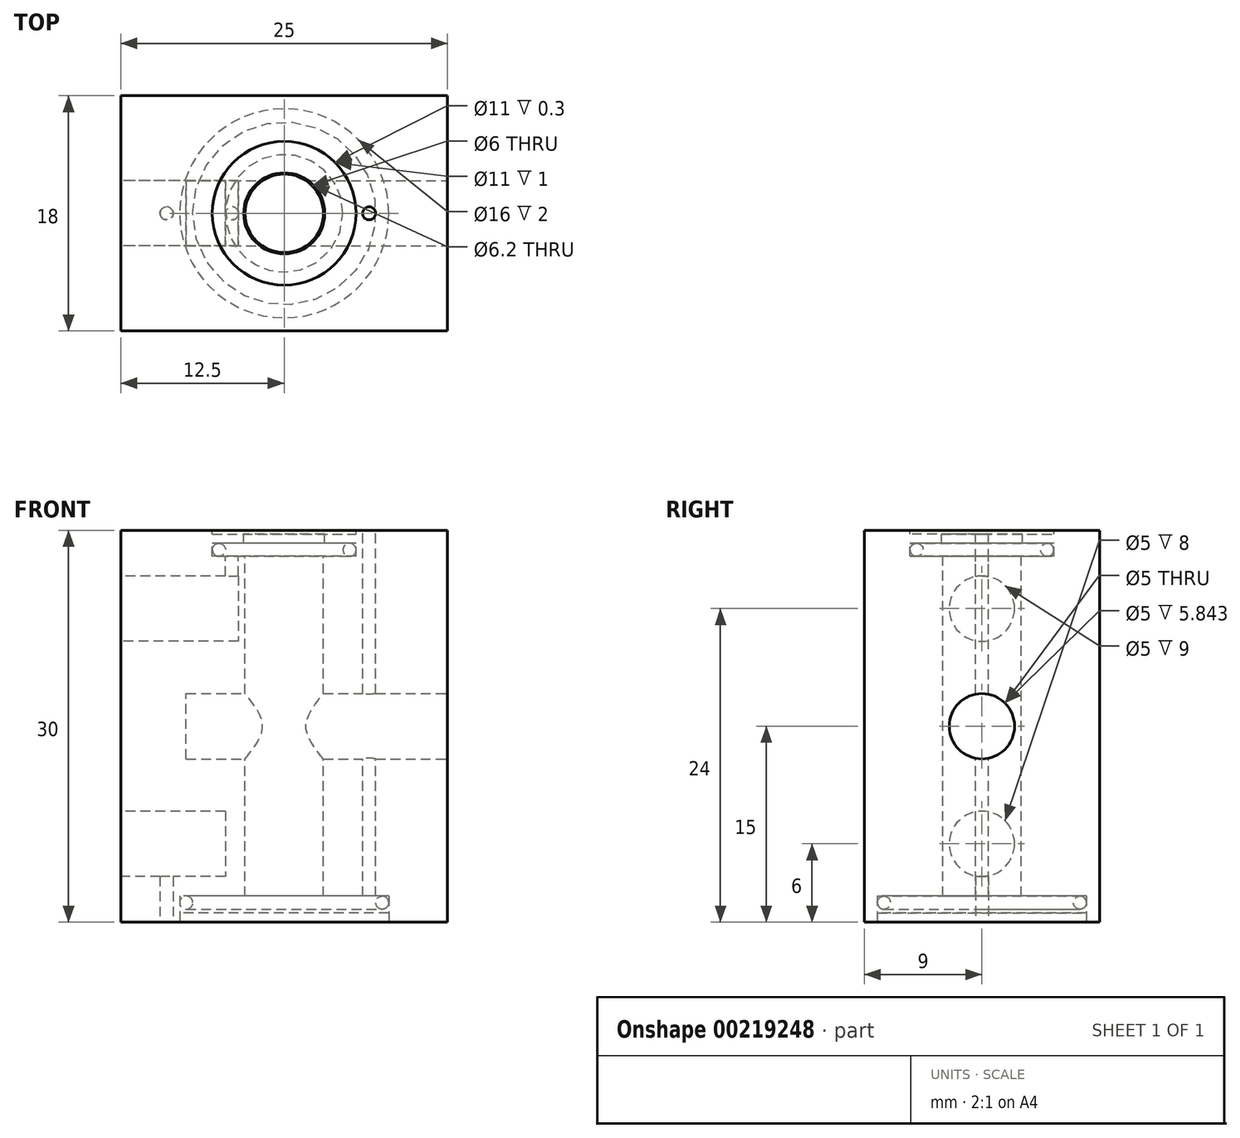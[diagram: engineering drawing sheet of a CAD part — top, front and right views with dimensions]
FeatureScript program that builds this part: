
annotation { "Feature Type Name" : "Feature", "Feature Type Description" : "" }
export const myFeature = defineFeature(function(context is Context, id is Id, definition is map)
    precondition{}
    {
        {
            var Q0;
            Q0=qCreatedBy(makeId("Front.planeOp"),FACE);
            var sketch = newSketch(context, id + "F0", { "sketchPlane" : qUnion([Q0])});
            skLineSegment(sketch, "E0.bottom", {"start": v(0, 0) * mm, "end": v(25, 0) * mm});
            skLineSegment(sketch, "E0.top", {"start": v(0, 30) * mm, "end": v(25, 30) * mm});
            skLineSegment(sketch, "E0.left", {"start": v(0, 0) * mm, "end": v(0, 30) * mm});
            skLineSegment(sketch, "E0.right", {"start": v(25, 0) * mm, "end": v(25, 30) * mm});
            skSolve(sketch);
        }
        {
            var Q0;
            Q0 = qSketchRegion(id + "F0", true);
            extrude(context, id + "F1", {"entities" : qUnion([Q0]), "endBound" : BoundingType.SYMMETRIC, "depth" : 18 * mm});
        }
        {
            var Q0;
            Q0=makeQuery(id+"F1.opExtrude","SWEPT_FACE",FACE,{"disambiguationData":[OSD([sQuery(id+"F0.wireOp",EDGE,"E0.right")])]});
            var sketch = newSketch(context, id + "F12", { "sketchPlane" : qUnion([Q0])});
            skLineSegment(sketch, "E1", {"start": v(0, 30) * mm, "end": v(0, 0) * mm, "construction": true});
            skCircle(sketch, "E2", {"center": v(0, 15) * mm, "radius": 2.5 * mm});
            skSolve(sketch);
        }
        {
            var Q0;
            Q0 = qSketchRegion(id + "F12", true);
            extrude(context, id + "F2", {"entities" : qUnion([Q0]), "operationType" : NewBodyOperationType.REMOVE, "oppositeDirection" : true, "depth" : 20 * mm});
        }
        {
            var Q0;
            Q0=makeQuery(id+"F1.opExtrude","SWEPT_FACE",FACE,{"disambiguationData":[OSD([sQuery(id+"F0.wireOp",EDGE,"E0.top")])]});
            var sketch = newSketch(context, id + "F13", { "sketchPlane" : qUnion([Q0])});
            skLineSegment(sketch, "E3", {"start": v(0, 0) * mm, "end": v(25, 0) * mm, "construction": true});
            skCircle(sketch, "E4", {"center": v(12.5, 0) * mm, "radius": 3 * mm});
            skCircle(sketch, "E5", {"center": v(19, 0) * mm, "radius": 0.5 * mm});
            skCircle(sketch, "E6", {"center": v(8.5, 0) * mm, "radius": 0.5 * mm});
            skCircle(sketch, "E7", {"center": v(12.5, 0) * mm, "radius": 8 * mm});
            skCircle(sketch, "E8", {"center": v(12.5, 0) * mm, "radius": 5.5 * mm});
            skSolve(sketch);
        }
        {
            var Q0;
            Q0=makeQuery(id+"F13.imprint","IMPRINT",FACE,{"disambiguationData":[TD([[makeQuery(id+"F13.imprint","IMPRINT",EDGE,{"derivedFrom":sQuery(id+"F13.wireOp",EDGE,"E4")}),1.0]])]});
            extrude(context, id + "F3", {"entities" : qUnion([Q0]), "operationType" : NewBodyOperationType.REMOVE, "endBound" : BoundingType.THROUGH_ALL, "oppositeDirection" : true, "depth" : 25 * mm});
        }
        {
            var Q0;
            Q0=makeQuery(id+"F13.imprint","IMPRINT",FACE,{"disambiguationData":[TD([[makeQuery(id+"F13.imprint","IMPRINT",EDGE,{"derivedFrom":sQuery(id+"F13.wireOp",EDGE,"E5")}),1.0]])]});
            var Q1;
            Q1=sQuery(id+"F13.wireOp",EDGE,"E5");
            extrude(context, id + "F14", {"entities" : qUnion([Q0]), "operationType" : NewBodyOperationType.REMOVE, "surfaceEntities" : qUnion([Q1]), "endBound" : BoundingType.THROUGH_ALL, "oppositeDirection" : true, "depth" : 25 * mm});
        }
        {
            var Q0;
            Q0=makeQuery(id+"F1.opExtrude","SWEPT_FACE",FACE,{"disambiguationData":[OSD([sQuery(id+"F0.wireOp",EDGE,"E0.left")])]});
            var sketch = newSketch(context, id + "F4", { "sketchPlane" : qUnion([Q0])});
            skLineSegment(sketch, "E9", {"start": v(0, 30) * mm, "end": v(0, 0) * mm, "construction": true});
            skCircle(sketch, "E10", {"center": v(0, 6) * mm, "radius": 2.5 * mm});
            skCircle(sketch, "E11", {"center": v(0, 24) * mm, "radius": 2.5 * mm});
            skSolve(sketch);
        }
        {
            var Q0;
            Q0=makeQuery(id+"F4.imprint","IMPRINT",FACE,{"disambiguationData":[TD([[makeQuery(id+"F4.imprint","IMPRINT",EDGE,{"derivedFrom":sQuery(id+"F4.wireOp",EDGE,"E10")}),1.0]])]});
            var Q1;
            Q1=sQuery(id+"F4.wireOp",EDGE,"E10");
            extrude(context, id + "F5", {"entities" : qUnion([Q0]), "operationType" : NewBodyOperationType.REMOVE, "surfaceEntities" : qUnion([Q1]), "oppositeDirection" : true, "depth" : 8 * mm});
        }
        {
            var Q0;
            Q0=qCreatedBy(makeId("Top.planeOp"),FACE);
            var sketch = newSketch(context, id + "F6", { "sketchPlane" : qUnion([Q0])});
            skCircle(sketch, "E12", {"center": v(3.5, 0) * mm, "radius": 0.5 * mm});
            skCircle(sketch, "E13.0", {"center": v(12.5, 0) * mm, "radius": 8 * mm});
            skSolve(sketch);
        }
        {
            var Q0;
            Q0=makeQuery(id+"F6.imprint","IMPRINT",FACE,{"disambiguationData":[TD([[makeQuery(id+"F6.imprint","IMPRINT",EDGE,{"derivedFrom":sQuery(id+"F6.wireOp",EDGE,"E12")}),1.0]])]});
            extrude(context, id + "F15", {"entities" : qUnion([Q0]), "operationType" : NewBodyOperationType.REMOVE, "endBound" : BoundingType.UP_TO_NEXT, "depth" : 25 * mm});
        }
        {
            var Q0;
            Q0=makeQuery(id+"F4.imprint","IMPRINT",FACE,{"disambiguationData":[TD([[makeQuery(id+"F4.imprint","IMPRINT",EDGE,{"derivedFrom":sQuery(id+"F4.wireOp",EDGE,"E11")}),1.0]])]});
            var Q1;
            Q1=sQuery(id+"F4.wireOp",EDGE,"E11");
            extrude(context, id + "F7", {"entities" : qUnion([Q0]), "operationType" : NewBodyOperationType.REMOVE, "surfaceEntities" : qUnion([Q1]), "oppositeDirection" : true, "depth" : 9 * mm});
        }
        {
            var Q0;
            Q0=makeQuery(id+"F13.imprint","IMPRINT",FACE,{"disambiguationData":[TD([[makeQuery(id+"F13.imprint","IMPRINT",EDGE,{"derivedFrom":sQuery(id+"F13.wireOp",EDGE,"E6")}),1.0]])]});
            extrude(context, id + "F16", {"entities" : qUnion([Q0]), "operationType" : NewBodyOperationType.REMOVE, "endBound" : BoundingType.UP_TO_NEXT, "oppositeDirection" : true, "depth" : 25 * mm});
        }
        {
            var Q0;
            Q0=makeQuery(id+"F13.imprint","IMPRINT",FACE,{"disambiguationData":[TD([[makeQuery(id+"F13.imprint","IMPRINT",EDGE,{"derivedFrom":sQuery(id+"F13.wireOp",EDGE,"E4")}),-1.0]])]});
            var Q1;
            Q1=sQuery(id+"F13.wireOp",EDGE,"E8");
            extrude(context, id + "F8", {"entities" : qUnion([Q0]), "operationType" : NewBodyOperationType.REMOVE, "surfaceEntities" : qUnion([Q1]), "oppositeDirection" : true, "depth" : 2 * mm});
        }
        {
            var Q0;
            Q0=makeQuery(id+"F6.imprint","IMPRINT",FACE,{"disambiguationData":[TD([[makeQuery(id+"F6.imprint","IMPRINT",EDGE,{"derivedFrom":sQuery(id+"F6.wireOp",EDGE,"E13.0")}),1.0]])]});
            var Q1;
            Q1=sQuery(id+"F6.wireOp",EDGE,"E13.0");
            extrude(context, id + "F9", {"entities" : qUnion([Q0]), "operationType" : NewBodyOperationType.REMOVE, "surfaceEntities" : qUnion([Q1]), "depth" : 2 * mm});
        }
        {
            var Q0;
            Q0=qCreatedBy(makeId("Front.planeOp"),FACE);
            var sketch = newSketch(context, id + "F10", { "sketchPlane" : qUnion([Q0])});
            skLineSegment(sketch, "E14", {"start": v(18, 30) * mm, "end": v(18, 28) * mm, "construction": true});
            skLineSegment(sketch, "E15", {"start": v(7, 28.5) * mm, "end": v(7, 30) * mm, "construction": true});
            skLineSegment(sketch, "E16.0.0", {"start": v(9.5, 28) * mm, "end": v(15.5, 28) * mm, "construction": true});
            skPoint(sketch, "E17.visualSharp", {"position": v(7, 28) * mm});
            skArc(sketch, "E17.filletArc", {"start": v(7, 28.5) * mm, "mid": v(7.15, 28.15) * mm, "end": v(7.5, 28) * mm, "construction": true});
            skCircle(sketch, "E18", {"center": v(7.5, 28.5) * mm, "radius": 0.5 * mm});
            skLineSegment(sketch, "E19", {"start": v(7, 30) * mm, "end": v(18, 30) * mm, "construction": true});
            skLineSegment(sketch, "E20", {"start": v(15.5, 28) * mm, "end": v(15.5, 2) * mm, "construction": true});
            skLineSegment(sketch, "E21", {"start": v(9.5, 2) * mm, "end": v(9.5, 28) * mm, "construction": true});
            skLineSegment(sketch, "E22", {"start": v(7, 28) * mm, "end": v(18, 28) * mm, "construction": true});
            skPoint(sketch, "E23.orphan", {"position": v(18, 28) * mm});
            skLineSegment(sketch, "E24", {"start": v(12.5, 30) * mm, "end": v(12.5, 28) * mm, "construction": true});
            skLineSegment(sketch, "E25", {"start": v(4.5, 0) * mm, "end": v(4.5, 1.94) * mm, "construction": true});
            skLineSegment(sketch, "E26", {"start": v(20.5, 2) * mm, "end": v(20.5, 0) * mm, "construction": true});
            skLineSegment(sketch, "E27", {"start": v(9.5, 2) * mm, "end": v(15.5, 2) * mm, "construction": true});
            skLineSegment(sketch, "E28", {"start": v(9.5, 2) * mm, "end": v(4.5, 2) * mm, "construction": true});
            skLineSegment(sketch, "E29", {"start": v(20.5, 0) * mm, "end": v(4.5, 0) * mm, "construction": true});
            skLineSegment(sketch, "E30", {"start": v(12.5, 0) * mm, "end": v(12.5, 2) * mm, "construction": true});
            skPoint(sketch, "E31.visualSharp", {"position": v(4.5, 2) * mm});
            skArc(sketch, "E31.filletArc", {"start": v(5, 2) * mm, "mid": v(4.65, 1.85) * mm, "end": v(4.5, 1.5) * mm, "construction": true});
            skCircle(sketch, "E32", {"center": v(5, 1.5) * mm, "radius": 0.5 * mm});
            skLineSegment(sketch, "E33", {"start": v(7, 29) * mm, "end": v(9.4, 29) * mm});
            skPoint(sketch, "E33.endSnap0", {"position": v(18, 29) * mm});
            skLineSegment(sketch, "E34", {"start": v(7, 29) * mm, "end": v(7, 29.7) * mm});
            skLineSegment(sketch, "E35", {"start": v(7, 29.7) * mm, "end": v(9.4, 29.7) * mm});
            skLineSegment(sketch, "E36", {"start": v(18, 29.7) * mm, "end": v(18, 29) * mm});
            skLineSegment(sketch, "E37", {"start": v(9.4, 29.7) * mm, "end": v(9.4, 29) * mm});
            skLineSegment(sketch, "E38.trimOffspring", {"start": v(12.5, 29.7) * mm, "end": v(18, 29.7) * mm});
            skLineSegment(sketch, "E39.trimOffspring", {"start": v(12.5, 29) * mm, "end": v(18, 29) * mm});
            skLineSegment(sketch, "E40", {"start": v(12.52, 1) * mm, "end": v(12.5, 1) * mm});
            skSolve(sketch);
        }
        {
            var Q0;
            Q0=makeQuery(id+"F10.imprint","IMPRINT",FACE,{"disambiguationData":[TD([[makeQuery(id+"F10.imprint","IMPRINT",EDGE,{"derivedFrom":sQuery(id+"F10.wireOp",EDGE,"E18")}),1.0]])]});
            var Q1;
            Q1=sQuery(id+"F10.wireOp",EDGE,"E24");
            revolve(context, id + "F17", {"entities" : qUnion([Q0]), "axis" : qUnion([Q1]), "revolveType" : RevolveType.FULL});
        }
        {
            var Q0;
            {var subQ0=sQuery(id+"F10.wireOp",EDGE,"E34");Q0=makeQuery(id+"F10.imprint","IMPRINT",FACE,{"disambiguationData":[TD([[makeQuery(id+"F10.imprint","IMPRINT",EDGE,{"derivedFrom":subQ0}),-1.0]])]});}
            var Q1;
            Q1=sQuery(id+"F10.wireOp",EDGE,"E24");
            revolve(context, id + "F18", {"operationType" : NewBodyOperationType.ADD, "entities" : qUnion([Q0]), "axis" : qUnion([Q1]), "revolveType" : RevolveType.FULL});
        }
        {
            var Q0;
            Q0=makeQuery(id+"F10.imprint","IMPRINT",FACE,{"disambiguationData":[TD([[makeQuery(id+"F10.imprint","IMPRINT",EDGE,{"derivedFrom":sQuery(id+"F10.wireOp",EDGE,"E32")}),1.0]])]});
            var Q1;
            Q1=sQuery(id+"F10.wireOp",EDGE,"E30");
            revolve(context, id + "F19", {"entities" : qUnion([Q0]), "axis" : qUnion([Q1]), "revolveType" : RevolveType.FULL});
        }
        {
            var Q0;
            Q0=makeQuery(id+"F6.imprint","IMPRINT",FACE,{"disambiguationData":[TD([[makeQuery(id+"F6.imprint","IMPRINT",EDGE,{"derivedFrom":sQuery(id+"F6.wireOp",EDGE,"E13.0")}),1.0]])]});
            var Q1;
            Q1=sQuery(id+"F6.wireOp",EDGE,"E13.0");
            var Q2;
            Q2=makeQuery(id+"F19.opRevolve","SWEPT_BODY",BODY,{"disambiguationData":[OSD([sQuery(id+"F10.wireOp",EDGE,"E32")])]});
            extrude(context, id + "F11", {"entities" : qUnion([Q0]), "surfaceEntities" : qUnion([Q1]), "endBoundEntityBody" : qUnion([Q2]), "depth" : 0.7 * mm});
        }
    });
